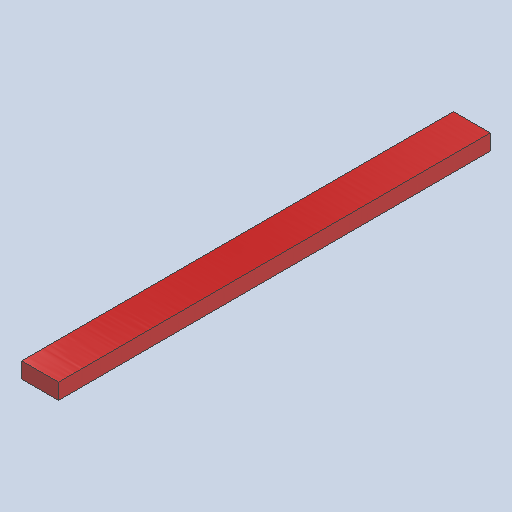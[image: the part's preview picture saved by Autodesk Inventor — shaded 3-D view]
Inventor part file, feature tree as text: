
AUTODESK INVENTOR PART (.ipt)
format: ipt  version: 2025 (Build 290162000, 162)  size: 97,792 bytes
history: native  units: in
note: dims shown in document units (in); Inventor stores cm internally (conversion verified against a paired STEP export)
features: other x4, sketch x1, plane x1
ambient origin geometry x8: Origin, YZ Plane, XZ Plane, XY Plane, X Axis, Y Axis, Z Axis, Center Point
bodies: Solid1 (feature_tree)
feature tree (6):
  other  "3'5x2x4_MIR.ipt"
  other  "Solid1::3'5x2x4_MIR.ipt"
  other  "TaggingFeature1"
  sketch  "Sketch1"  dims[d0=0.3937in]
  plane  "Work Plane1"
  other  "Finish1"
